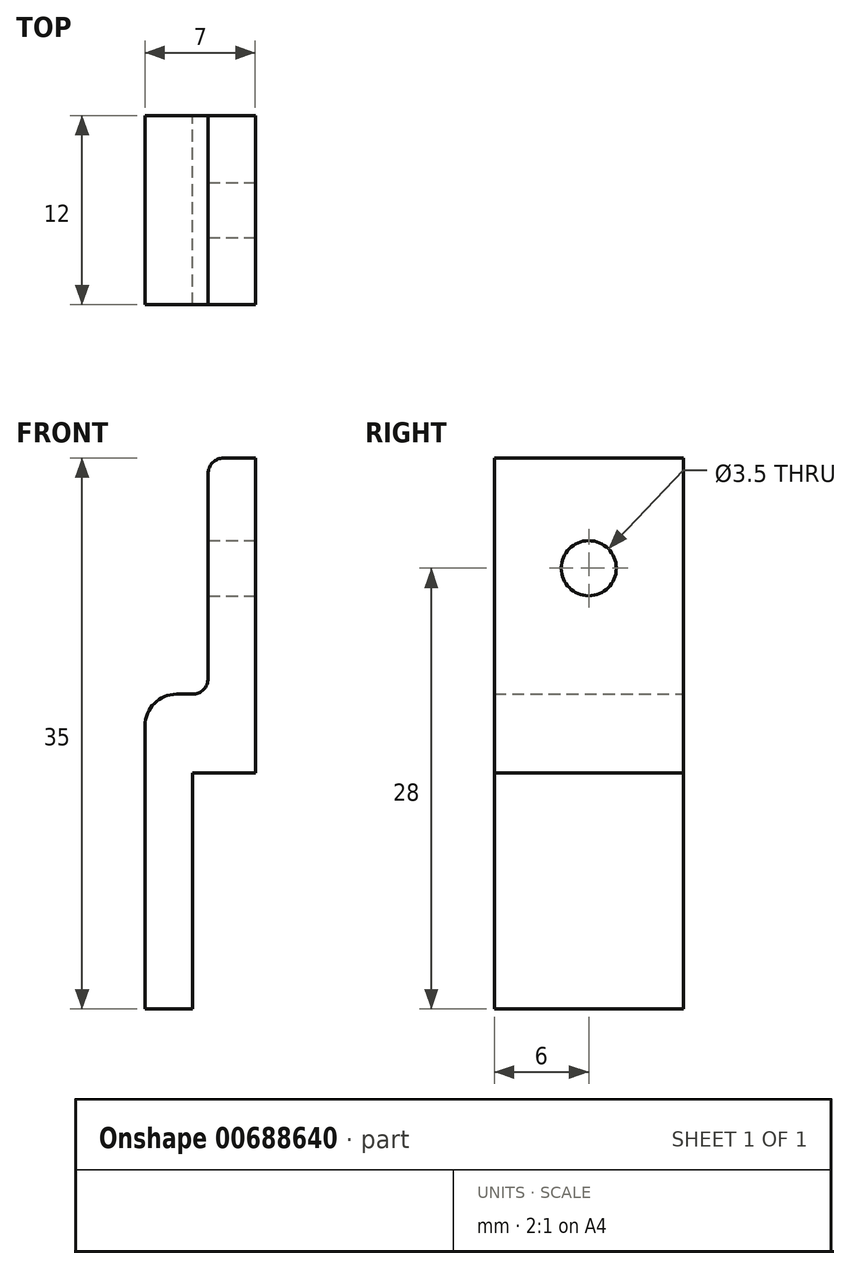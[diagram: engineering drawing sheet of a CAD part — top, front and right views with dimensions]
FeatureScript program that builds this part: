
annotation { "Feature Type Name" : "Feature", "Feature Type Description" : "" }
export const myFeature = defineFeature(function(context is Context, id is Id, definition is map)
    precondition{}
    {
        {
            var Q0;
            Q0=qCreatedBy(makeId("Front.planeOp"),FACE);
            var sketch = newSketch(context, id + "F0", { "sketchPlane" : qUnion([Q0])});
            skLineSegment(sketch, "E0", {"start": v(-25.7, 0) * mm, "end": v(-25.7, 15) * mm});
            skLineSegment(sketch, "E1", {"start": v(-25.7, 15) * mm, "end": v(-21.7, 15) * mm});
            skLineSegment(sketch, "E2", {"start": v(-21.7, 15) * mm, "end": v(-21.7, 35) * mm});
            skLineSegment(sketch, "E3", {"start": v(-21.7, 35) * mm, "end": v(-23.7, 35) * mm});
            skLineSegment(sketch, "E4", {"start": v(-24.7, 34) * mm, "end": v(-24.7, 21) * mm});
            skLineSegment(sketch, "E5", {"start": v(-25.7, 20) * mm, "end": v(-26.7, 20) * mm});
            skLineSegment(sketch, "E6", {"start": v(-28.7, 18) * mm, "end": v(-28.7, 0) * mm});
            skLineSegment(sketch, "E7", {"start": v(-28.7, 0) * mm, "end": v(-25.7, 0) * mm});
            skPoint(sketch, "E8.visualSharp", {"position": v(-24.7, 35) * mm});
            skArc(sketch, "E8.filletArc", {"start": v(-23.7, 35) * mm, "mid": v(-24.4, 34.7) * mm, "end": v(-24.7, 34) * mm});
            skPoint(sketch, "E9.visualSharp", {"position": v(-28.7, 20) * mm});
            skArc(sketch, "E9.filletArc", {"start": v(-26.7, 20) * mm, "mid": v(-28.11, 19.41) * mm, "end": v(-28.7, 18) * mm});
            skPoint(sketch, "E10.visualSharp", {"position": v(-24.7, 20) * mm});
            skArc(sketch, "E10.filletArc", {"start": v(-25.7, 20) * mm, "mid": v(-25, 20.3) * mm, "end": v(-24.7, 21) * mm});
            skSolve(sketch);
        }
        {
            var Q0;
            Q0=makeQuery(id+"F0.imprint","IMPRINT",FACE,{"disambiguationData":[TD([[makeQuery(id+"F0.imprint","IMPRINT",EDGE,{"derivedFrom":sQuery(id+"F0.wireOp",EDGE,"E0")}),1.0]])]});
            extrude(context, id + "F1", {"entities" : qUnion([Q0]), "depth" : 12 * mm, "offsetDistance" : 25 * mm});
        }
        {
            var Q0;
            Q0=makeQuery(id+"F1.opExtrude","SWEPT_FACE",FACE,{"disambiguationData":[OSD([sQuery(id+"F0.wireOp",EDGE,"E2")])]});
            var sketch = newSketch(context, id + "F2", { "sketchPlane" : qUnion([Q0])});
            skCircle(sketch, "E11", {"center": v(-6, 28) * mm, "radius": 1.75 * mm});
            skPoint(sketch, "E11.centerSnap0", {"position": v(-6, 35) * mm});
            skSolve(sketch);
        }
        {
            var Q0;
            Q0=makeQuery(id+"F2.imprint","IMPRINT",FACE,{"disambiguationData":[TD([[makeQuery(id+"F2.imprint","IMPRINT",EDGE,{"derivedFrom":sQuery(id+"F2.wireOp",EDGE,"E11")}),1.0]])]});
            extrude(context, id + "F3", {"entities" : qUnion([Q0]), "operationType" : NewBodyOperationType.REMOVE, "endBound" : BoundingType.THROUGH_ALL, "oppositeDirection" : true, "depth" : 25 * mm, "offsetDistance" : 25 * mm});
        }
    });
